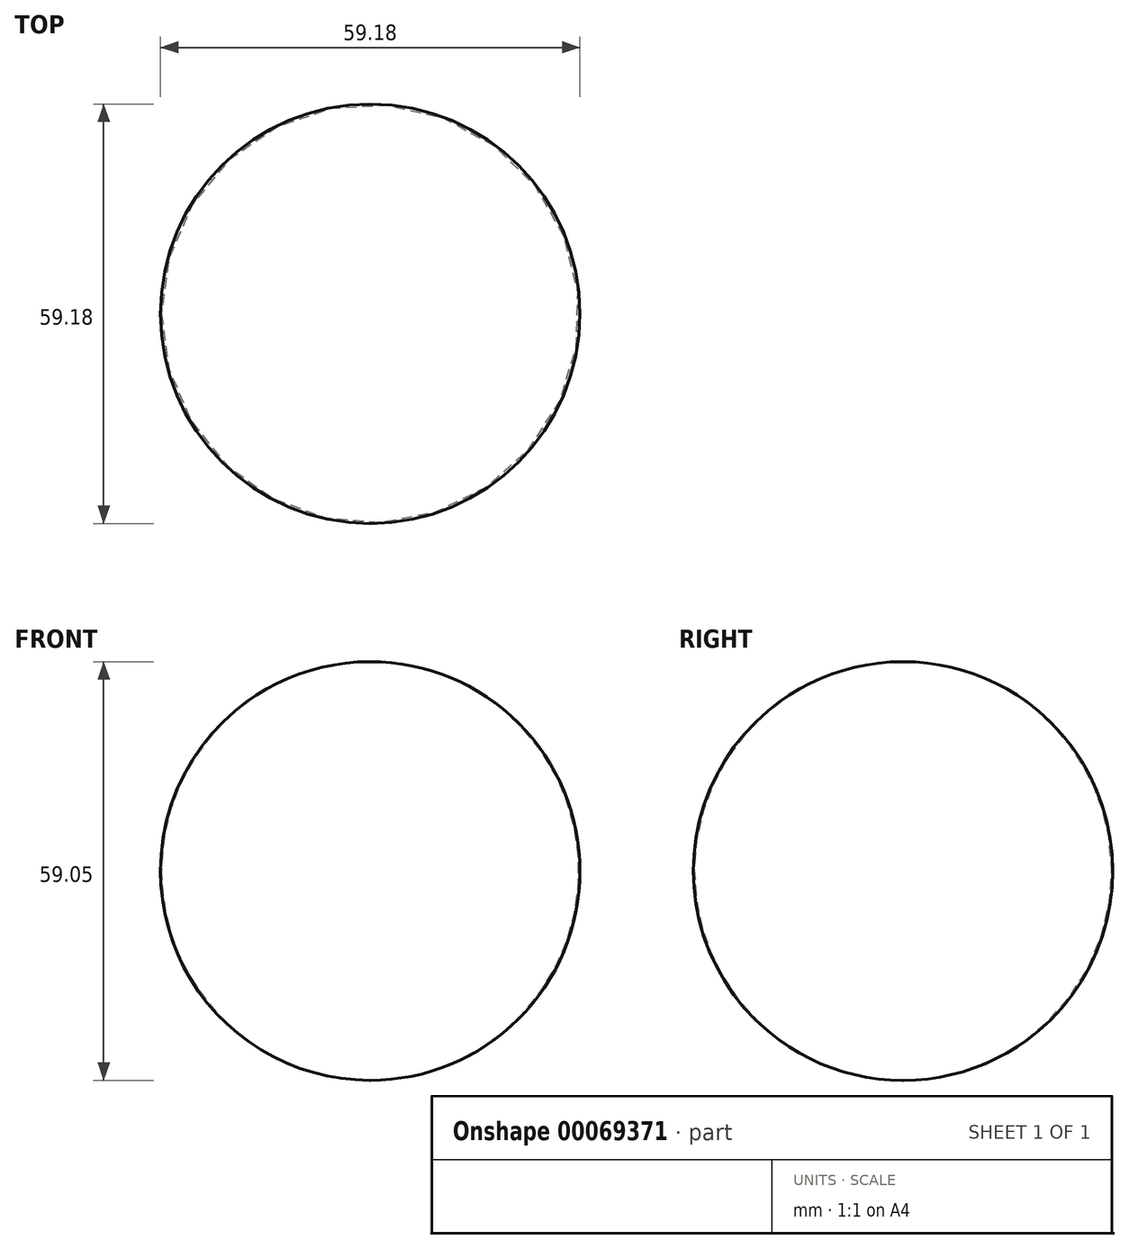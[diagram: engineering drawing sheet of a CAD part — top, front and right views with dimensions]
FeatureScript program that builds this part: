
annotation { "Feature Type Name" : "Feature", "Feature Type Description" : "" }
export const myFeature = defineFeature(function(context is Context, id is Id, definition is map)
    precondition{}
    {
        {
            var Q0;
            Q0=qCreatedBy(makeId("Front.planeOp"),FACE);
            var sketch = newSketch(context, id + "F0", { "sketchPlane" : qUnion([Q0])});
            skLineSegment(sketch, "E0", {"start": v(0, 30.38) * mm, "end": v(0, -28.67) * mm});
            skArc(sketch, "E1", {"start": v(0, -28.67) * mm, "mid": v(29.45, 0.86) * mm, "end": v(0, 30.38) * mm});
            skSolve(sketch);
        }
        {
            var Q0;
            Q0 = qSketchRegion(id + "F0", true);
            var Q1;
            Q1=sQuery(id+"F0.wireOp",EDGE,"E0");
            revolve(context, id + "F1", {"entities" : qUnion([Q0]), "axis" : qUnion([Q1]), "revolveType" : RevolveType.FULL});
        }
    });
